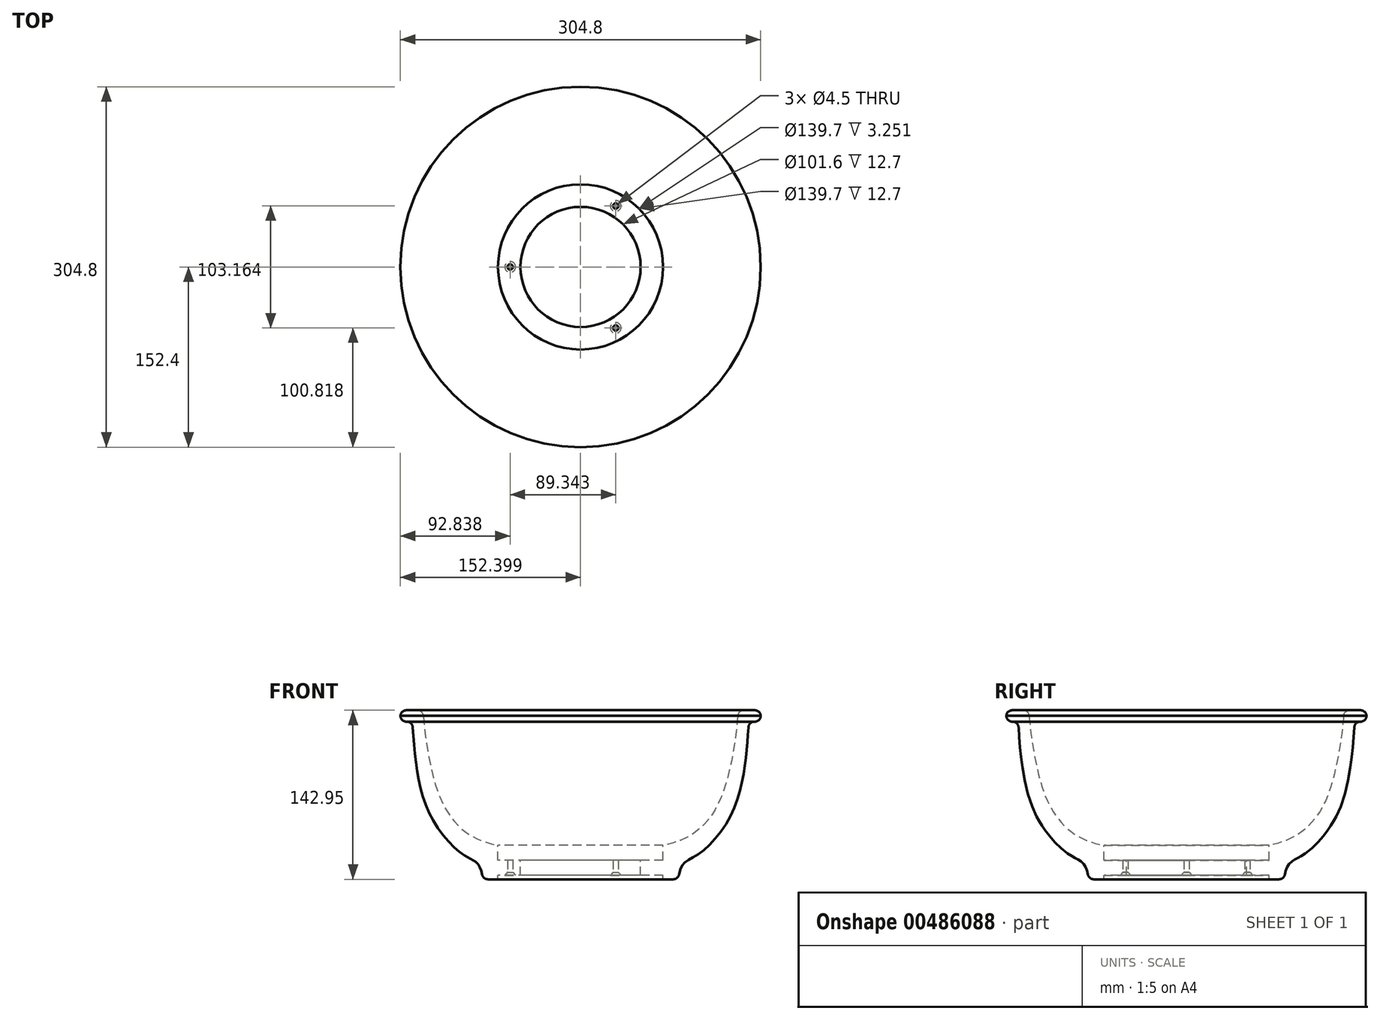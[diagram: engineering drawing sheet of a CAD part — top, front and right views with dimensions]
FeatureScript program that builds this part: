
annotation { "Feature Type Name" : "Feature", "Feature Type Description" : "" }
export const myFeature = defineFeature(function(context is Context, id is Id, definition is map)
    precondition{}
    {
        {
            var Q0;
            Q0=qCreatedBy(makeId("Front.planeOp"),FACE);
            var sketch = newSketch(context, id + "F0", { "sketchPlane" : qUnion([Q0])});
            skLineSegment(sketch, "E0", {"start": v(35.64, -39.13) * mm, "end": v(16.59, -39.13) * mm});
            skLineSegment(sketch, "E1", {"start": v(16.59, -39.13) * mm, "end": v(16.59, -26.43) * mm});
            skLineSegment(sketch, "E2", {"start": v(-46.91, 87.87) * mm, "end": v(-65.96, 87.87) * mm});
            skLineSegment(sketch, "E3", {"start": v(-65.96, 87.87) * mm, "end": v(-65.96, 78.22) * mm});
            skLineSegment(sketch, "E4", {"start": v(-65.96, 78.22) * mm, "end": v(-55.8, 78.22) * mm});
            skLineSegment(sketch, "E5", {"start": v(3.89, -55.08) * mm, "end": v(16.59, -55.08) * mm});
            skLineSegment(sketch, "E6", {"start": v(16.59, -55.08) * mm, "end": v(16.59, -51.83) * mm});
            skLineSegment(sketch, "E7", {"start": v(16.59, -51.83) * mm, "end": v(35.64, -51.83) * mm});
            skLineSegment(sketch, "E8", {"start": v(86.44, -62.05) * mm, "end": v(86.44, -60) * mm, "construction": true});
            skLineSegment(sketch, "E9", {"start": v(86.44, 67) * mm, "end": v(86.44, -60) * mm, "construction": true});
            skFitSpline(sketch, "E10", {"points": [v(-46.91, 87.87) * mm, v(-44.98, 68) * mm, v(-35.63, 22.9) * mm, v(-20.24, -6.21) * mm, v(16.59, -26.43) * mm], "startDerivative": vector(7.22, -90.77) * mm, "endDerivative": vector(206.92, -41.9) * mm});
            skFitSpline(sketch, "E11", {"points": [v(3.89, -55.08) * mm, v(0, -42.67) * mm, v(-12.84, -34.12) * mm, v(-40.03, -2.23) * mm, v(-52.7, 42.53) * mm, v(-55.8, 78.22) * mm], "startDerivative": vector(-18.47, 92.54) * mm, "endDerivative": vector(-9.11, 154.2) * mm});
            skLineSegment(sketch, "E12", {"start": v(86.44, -62.05) * mm, "end": v(86.44, 1.45) * mm, "construction": true});
            skPoint(sketch, "E13", {"position": v(86.44, -27.57) * mm});
            skLineSegment(sketch, "E14", {"start": v(35.64, -39.13) * mm, "end": v(35.64, -51.83) * mm});
            skSolve(sketch);
        }
        {
            var Q0;
            {var subQ1=sQuery(id+"F0.wireOp",EDGE,"E0");Q0=makeQuery(id+"F0.imprint","IMPRINT",FACE,{"disambiguationData":[TD([[makeQuery(id+"F0.imprint","IMPRINT",EDGE,{"derivedFrom":subQ1}),1.0]])]});}
            var Q1;
            Q1=sQuery(id+"F0.wireOp",EDGE,"E9");
            revolve(context, id + "F1", {"entities" : qUnion([Q0]), "axis" : qUnion([Q1]), "revolveType" : RevolveType.FULL});
        }
        {
            var Q0;
            Q0=makeQuery(id+"F1.opRevolve","SWEPT_FACE",FACE,{"disambiguationData":[OSD([sQuery(id+"F0.wireOp",EDGE,"E11")])]});
            var Q1;
            Q1=makeQuery(id+"F1.opRevolve","SWEPT_EDGE",EDGE,{"disambiguationData":[OSD([sQuery(id+"F0.wireOp",EDGE,"E3"),sQuery(id+"F0.wireOp",EDGE,"E4")])]});
            var Q2;
            Q2=makeQuery(id+"F1.opRevolve","SWEPT_EDGE",EDGE,{"disambiguationData":[OSD([sQuery(id+"F0.wireOp",EDGE,"E2"),sQuery(id+"F0.wireOp",EDGE,"E10")])]});
            fillet(context, id + "F2", {"entities" : qUnion([Q0, Q1, Q2]), "radius" : 5.08 * mm, "tangentPropagation" : true, "allowEdgeOverflow" : false});
        }
        {
            var Q0;
            Q0=makeQuery(id+"F1.opRevolve","SWEPT_EDGE",EDGE,{"disambiguationData":[OSD([sQuery(id+"F0.wireOp",EDGE,"E2"),sQuery(id+"F0.wireOp",EDGE,"E3")])]});
            fillet(context, id + "F3", {"entities" : qUnion([Q0]), "radius" : 5.08 * mm, "tangentPropagation" : true, "allowEdgeOverflow" : false});
        }
        {
            var Q0;
            Q0=makeQuery(id+"F1.opRevolve","SWEPT_FACE",FACE,{"disambiguationData":[OSD([sQuery(id+"F0.wireOp",EDGE,"E7")])]});
            var sketch = newSketch(context, id + "F4", { "sketchPlane" : qUnion([Q0])});
            skCircle(sketch, "E15", {"center": v(86.44, 0) * mm, "radius": 59.56 * mm, "construction": true});
            skPoint(sketch, "E16", {"position": v(26.88, 0) * mm});
            skPoint(sketch, "E17.1.0", {"position": v(116.22, -51.58) * mm});
            skPoint(sketch, "E17.2.0", {"position": v(116.22, 51.58) * mm});
            skSolve(sketch);
        }
        {
            var Q0;
            Q0=sQuery(id+"F4.wireOp",VERTEX,"E17.2.0");
            var Q1;
            Q1=sQuery(id+"F4.wireOp",VERTEX,"E17.1.0");
            var Q2;
            Q2=sQuery(id+"F4.wireOp",VERTEX,"E16");
            var Q3;
            Q3=makeQuery(id+"F1.opRevolve","SWEPT_BODY",BODY,{"disambiguationData":[OSD([sQuery(id+"F0.wireOp",EDGE,"a37a7dde-3c13-4033-8765-0b5ca1076a72"),sQuery(id+"F0.wireOp",EDGE,"E0"),sQuery(id+"F0.wireOp",EDGE,"E1"),sQuery(id+"F0.wireOp",EDGE,"E2"),sQuery(id+"F0.wireOp",EDGE,"E3"),sQuery(id+"F0.wireOp",EDGE,"E4"),sQuery(id+"F0.wireOp",EDGE,"E5"),sQuery(id+"F0.wireOp",EDGE,"E6"),sQuery(id+"F0.wireOp",EDGE,"E7"),sQuery(id+"F0.wireOp",EDGE,"E10"),sQuery(id+"F0.wireOp",EDGE,"E11")])]});
            hole(context, id + "F5", {"style" : HoleStyle.C_SINK, "endStyle" : HoleEndStyle.THROUGH, "standardTappedOrClearance" : lookupTablePath({ "standard" : "ANSI", "fit" : "Normal (ASME)", "size" : "#8", "type" : "Clearance" }), "standardBlindInLast" : lookupTablePath({ "fit" : "Free", "standard" : "ANSI", "size" : "#8", "type" : "Clearance" }), "holeDiameter" : 4.5 * mm, "cSinkDiameter" : 9.12 * mm, "cSinkAngle" : 82 * degree, "isTappedThrough" : true, "tappedDepth" : 12.7 * mm, "tapClearance" : 3, "locations" : qUnion([Q0, Q1, Q2]), "scope" : qUnion([Q3])});
        }
    });
